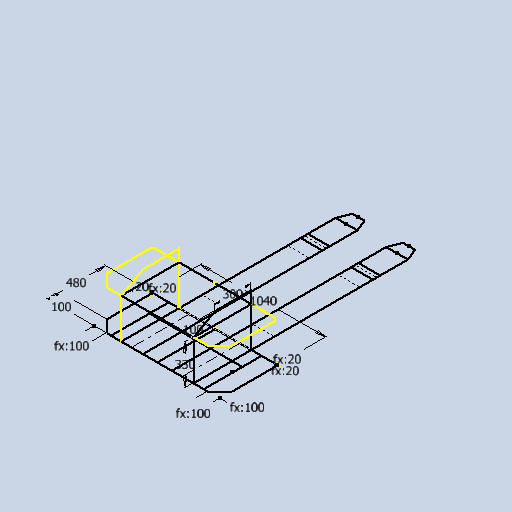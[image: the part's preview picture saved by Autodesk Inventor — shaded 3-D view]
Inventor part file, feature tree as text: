
AUTODESK INVENTOR PART (.ipt)
format: ipt  version: 2022.1 (Build 261234000, 234)  size: 144,384 bytes
history: native  units: mm
features: sketch x5, other x4, plane x3, reference x2
ambient origin geometry x8: Origin, YZ Plane, XZ Plane, XY Plane, X Axis, Y Axis, Z Axis, Center Point
feature tree (14):
  sketch  "Sketch1"  dims[d23=100.0mm]
  sketch  "Sketch2"  dims[d24=100.0mm]
  plane  "Plano de trabajo1"
  plane  "Plano de trabajo2"
  sketch  "Boceto3"  dims[d25=100.0mm]
  sketch  "Boceto4"  dims[d26=100.0mm]
  plane  "Plano de trabajo3"
  sketch  "Boceto5"  dims[d27=20.0mm d28=20.0mm d29=20.0mm d30=20.0mm d31=480.0mm d37=100.0mm d38=100.0mm d41=1400.0mm d42=30.0mm d43=30.0mm d44=85.0mm d45=85.0mm d47=300.0mm d48=-300.0mm d50=300.0mm d51=330.0mm d52=330.0mm d53=160.0mm d55=350.0mm d61=500.0mm d62=140.0mm d63=100.0mm]
  reference  "Referencia1"
  reference  "Referencia2"
  other  "EstructuraInferior - Soldadura.iam"
  other  "Frame_Base:1"
  other  "ISO 12633-2 40x40x5 - 3875.41:2"
  other  "ISO 12633-2 40x40x5 - 3875.41:1"
